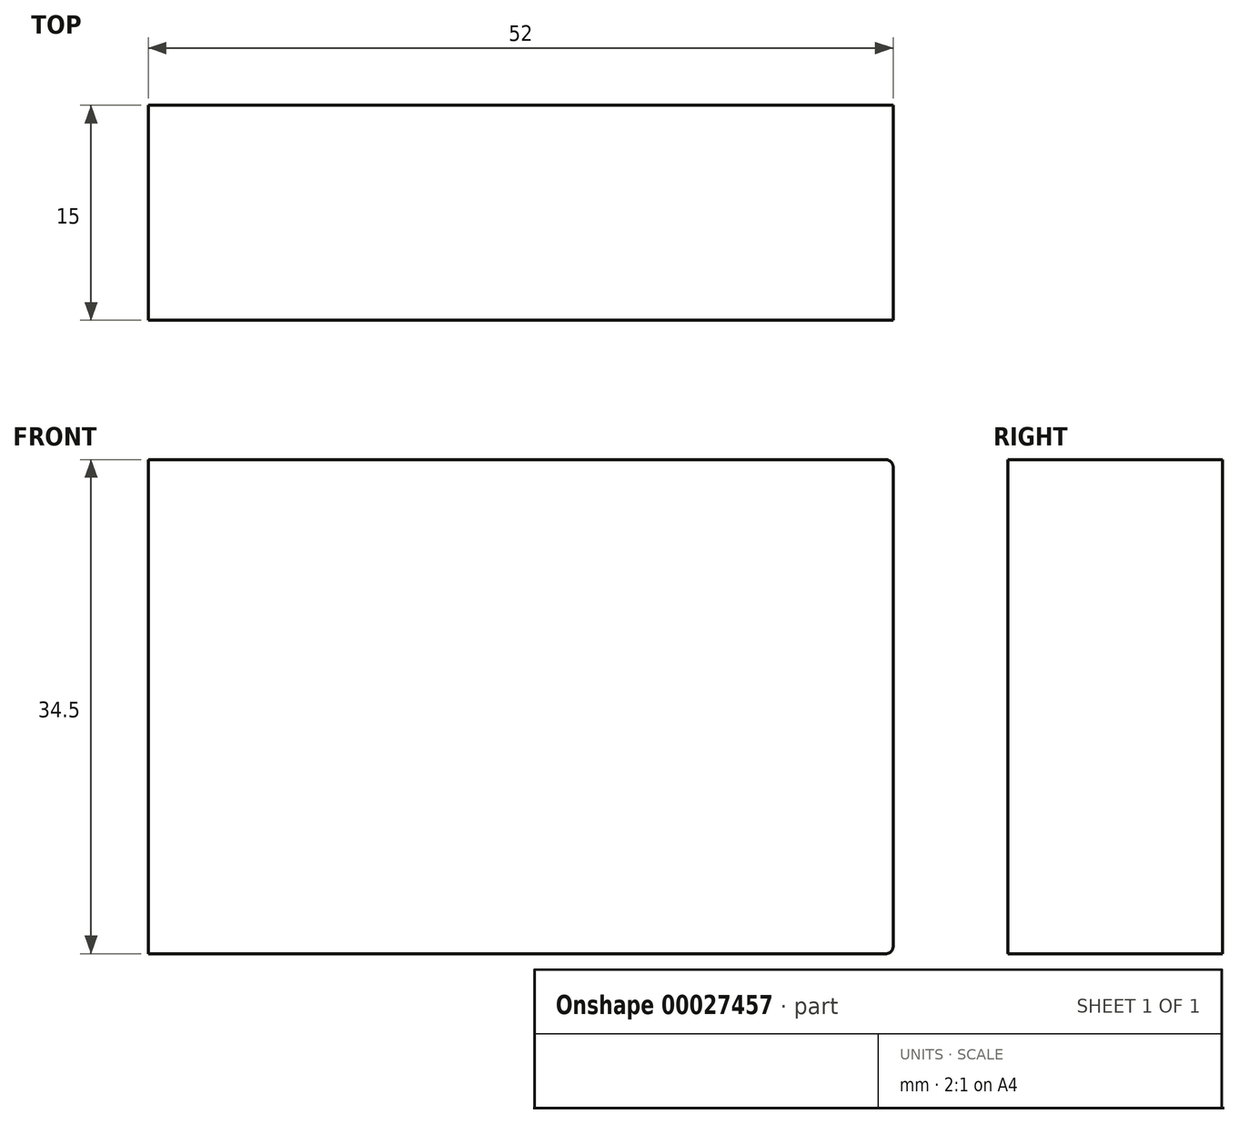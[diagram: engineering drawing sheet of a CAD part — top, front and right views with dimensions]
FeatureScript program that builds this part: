
annotation { "Feature Type Name" : "Feature", "Feature Type Description" : "" }
export const myFeature = defineFeature(function(context is Context, id is Id, definition is map)
    precondition{}
    {
        {
            var Q0;
            Q0=qCreatedBy(makeId("Front.planeOp"),FACE);
            var sketch = newSketch(context, id + "F0", { "sketchPlane" : qUnion([Q0])});
            skLineSegment(sketch, "E0.rect.bottom", {"start": v(26, 17.25) * mm, "end": v(-26, 17.25) * mm});
            skLineSegment(sketch, "E0.rect.top", {"start": v(26, -17.25) * mm, "end": v(-26, -17.25) * mm});
            skLineSegment(sketch, "E0.rect.left", {"start": v(26, 17.25) * mm, "end": v(26, -17.25) * mm});
            skLineSegment(sketch, "E0.rect.right", {"start": v(-26, 17.25) * mm, "end": v(-26, -17.25) * mm});
            skPoint(sketch, "E0.rect.middle", {"position": v(0, 0) * mm});
            skSolve(sketch);
        }
        {
            var Q0;
            Q0=makeQuery(id+"F0.imprint","IMPRINT",FACE,{"disambiguationData":[TD([[makeQuery(id+"F0.imprint","IMPRINT",EDGE,{"derivedFrom":sQuery(id+"F0.wireOp",EDGE,"E0.rect.bottom")}),1.0]])]});
            extrude(context, id + "F1", {"entities" : qUnion([Q0]), "depth" : 15 * mm});
        }
        {
            var Q0;
            Q0=makeQuery(id+"F1.opExtrude","SWEPT_EDGE",EDGE,{"disambiguationData":[OSD([sQuery(id+"F0.wireOp",EDGE,"E0.rect.top"),sQuery(id+"F0.wireOp",EDGE,"E0.rect.left")])]});
            var Q1;
            Q1=makeQuery(id+"F1.opExtrude","SWEPT_EDGE",EDGE,{"disambiguationData":[OSD([sQuery(id+"F0.wireOp",EDGE,"E0.rect.bottom"),sQuery(id+"F0.wireOp",EDGE,"E0.rect.left")])]});
            fillet(context, id + "F2", {"entities" : qUnion([Q0, Q1]), "radius" : .5 * mm, "tangentPropagation" : true, "allowEdgeOverflow" : false});
        }
    });
